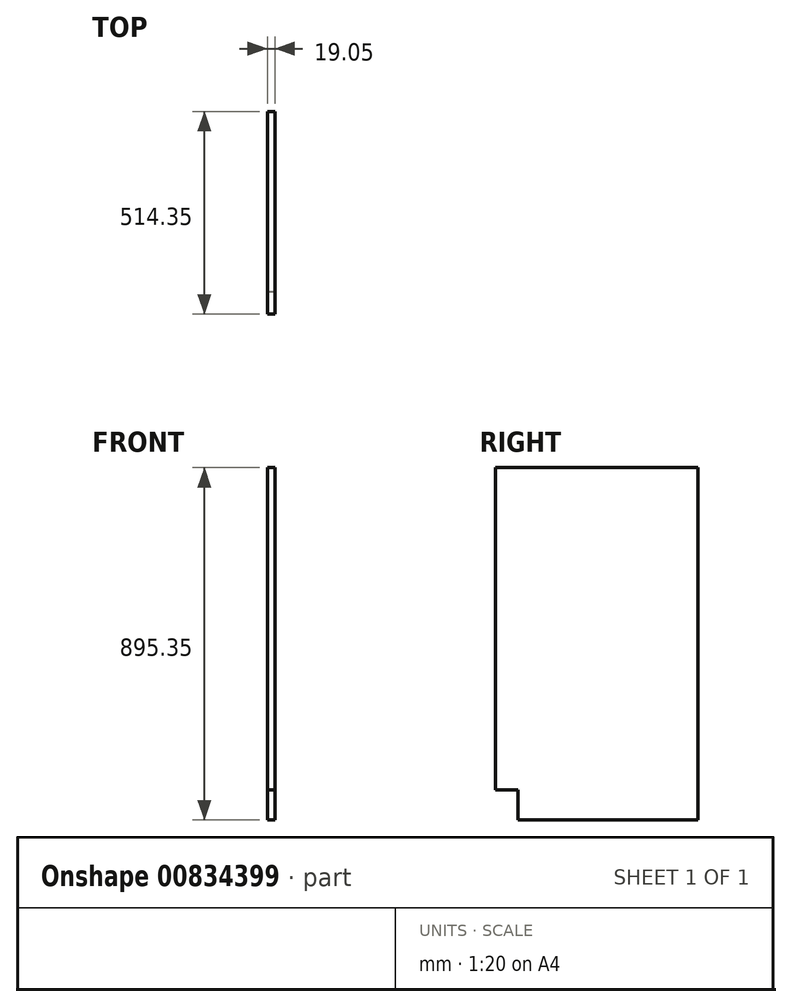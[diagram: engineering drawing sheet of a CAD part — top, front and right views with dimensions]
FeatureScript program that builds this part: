
annotation { "Feature Type Name" : "Feature", "Feature Type Description" : "" }
export const myFeature = defineFeature(function(context is Context, id is Id, definition is map)
    precondition{}
    {
        {
            var Q0;
            Q0=qCreatedBy(makeId("Right.planeOp"),FACE);
            var sketch = newSketch(context, id + "F0", { "sketchPlane" : qUnion([Q0])});
            skLineSegment(sketch, "E0.bottom", {"start": v(-192.62, 658.28) * mm, "end": v(321.73, 658.28) * mm});
            skLineSegment(sketch, "E0.top", {"start": v(-192.62, -160.87) * mm, "end": v(-135.47, -160.87) * mm});
            skLineSegment(sketch, "E0.left", {"start": v(-192.62, 658.28) * mm, "end": v(-192.62, -160.87) * mm});
            skLineSegment(sketch, "E0.right", {"start": v(321.73, 658.28) * mm, "end": v(321.73, -160.87) * mm});
            skLineSegment(sketch, "E1.bottom", {"start": v(-211.67, -160.87) * mm, "end": v(-135.47, -160.87) * mm});
            skLineSegment(sketch, "E1.right", {"start": v(-135.47, -160.87) * mm, "end": v(-135.47, -237.07) * mm});
            skLineSegment(sketch, "E2.top", {"start": v(-135.47, -237.07) * mm, "end": v(321.73, -237.07) * mm});
            skLineSegment(sketch, "E2.right", {"start": v(321.73, -160.87) * mm, "end": v(321.73, -237.07) * mm});
            skSolve(sketch);
        }
        {
            var Q0;
            Q0=makeQuery(id+"F0.imprint","IMPRINT",FACE,{"disambiguationData":[TD([[makeQuery(id+"F0.imprint","IMPRINT",EDGE,{"derivedFrom":sQuery(id+"F0.wireOp",EDGE,"E0.bottom")}),-1.0]])]});
            extrude(context, id + "F1", {"entities" : qUnion([Q0]), "oppositeDirection" : true, "depth" : 19.05 * mm, "offsetDistance" : 25.4 * mm});
        }
    });
